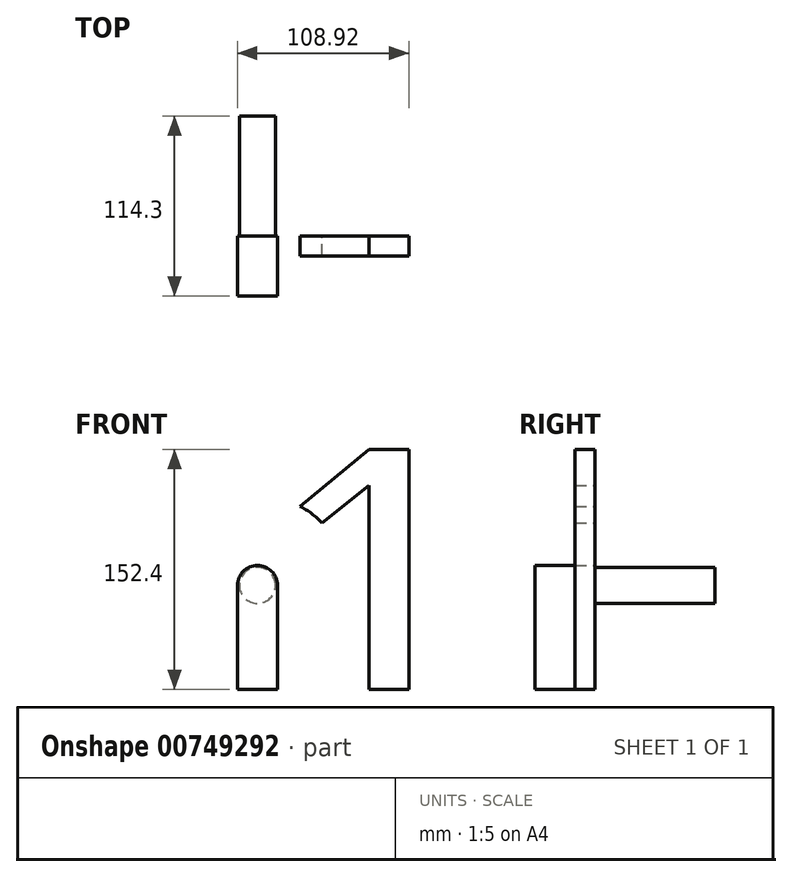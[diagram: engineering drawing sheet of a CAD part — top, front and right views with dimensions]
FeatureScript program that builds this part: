
annotation { "Feature Type Name" : "Feature", "Feature Type Description" : "" }
export const myFeature = defineFeature(function(context is Context, id is Id, definition is map)
    precondition{}
    {
        {
            var Q0;
            Q0=qCreatedBy(makeId("Front.planeOp"),FACE);
            var sketch = newSketch(context, id + "F0", { "sketchPlane" : qUnion([Q0])});
            skLineSegment(sketch, "E0", {"start": v(-9.03, 14.64) * mm, "end": v(34.6, 50.66) * mm});
            skLineSegment(sketch, "E1", {"start": v(4.97, 4) * mm, "end": v(49.46, 39.82) * mm});
            skLineSegment(sketch, "E2", {"start": v(34.6, 50.66) * mm, "end": v(34.6, -101.74) * mm});
            skLineSegment(sketch, "E3", {"start": v(34.6, -101.74) * mm, "end": v(60, -101.74) * mm});
            skLineSegment(sketch, "E4", {"start": v(60, -101.74) * mm, "end": v(60, 50.66) * mm});
            skLineSegment(sketch, "E5", {"start": v(60, 50.66) * mm, "end": v(34.6, 50.66) * mm});
            skArc(sketch, "E6", {"start": v(4.97, 4) * mm, "mid": v(-1.62, 9.86) * mm, "end": v(-9.03, 14.64) * mm});
            skPoint(sketch, "E7.orphan", {"position": v(-14.37, 10.24) * mm});
            skPoint(sketch, "E8.start.orphan", {"position": v(0, 0) * mm});
            skPoint(sketch, "E9.end.orphan", {"position": v(-72.43, -71.25) * mm});
            skArc(sketch, "E10", {"start": v(-72.43, -71.25) * mm, "mid": v(-0.59, -71.84) * mm, "end": v(0, 0) * mm});
            skCircle(sketch, "E11", {"center": v(-36.21, -35.63) * mm, "radius": 12.7 * mm});
            skLineSegment(sketch, "E12", {"start": v(34.6, -101.74) * mm, "end": v(-36.21, -101.74) * mm});
            skLineSegment(sketch, "E13", {"start": v(-36.21, -101.74) * mm, "end": v(-36.21, -47.06) * mm});
            skLineSegment(sketch, "E14", {"start": v(-48.91, -35.63) * mm, "end": v(-48.91, -101.74) * mm});
            skLineSegment(sketch, "E15", {"start": v(-48.91, -101.74) * mm, "end": v(-36.21, -101.74) * mm});
            skLineSegment(sketch, "E16", {"start": v(-23.51, -35.63) * mm, "end": v(-23.51, -101.74) * mm});
            skLineSegment(sketch, "E17", {"start": v(-48.91, -35.63) * mm, "end": v(-47.64, -35.63) * mm});
            skCircle(sketch, "E18", {"center": v(-36.21, -35.63) * mm, "radius": 11.43 * mm});
            skLineSegment(sketch, "E19.trimOffspring", {"start": v(-24.78, -35.63) * mm, "end": v(-23.51, -35.63) * mm});
            skSolve(sketch);
        }
        {
            var Q0;
            Q0 = qSketchRegion(id + "F0", true);
            extrude(context, id + "F1", {"entities" : qUnion([Q0]), "depth" : 12.7 * mm, "offsetDistance" : 25.4 * mm});
        }
        {
            var Q0;
            {var subQ5=sQuery(id+"F0.wireOp",EDGE,"E15");Q0=makeQuery(id+"F0.imprint","IMPRINT",FACE,{"disambiguationData":[TD([[makeQuery(id+"F0.imprint","IMPRINT",EDGE,{"derivedFrom":subQ5}),1.0]])]});}
            var Q1;
            {var subQ0=sQuery(id+"F0.wireOp",EDGE,"E16");var subQ1=sQuery(id+"F0.wireOp",EDGE,"E10");var subQ2=makeQuery(id+"F0.imprint","INTERSECT",VERTEX,{"derivedFrom":[subQ1,subQ0]});Q1=makeQuery(id+"F0.imprint","IMPRINT",FACE,{"disambiguationData":[TD([[makeQuery(id+"F0.imprint","IMPRINT",EDGE,{"disambiguationData":[TD([[subQ2,1.0]])],"derivedFrom":subQ1}),-1.0]])]});}
            var Q2;
            {var subQ0=sQuery(id+"F0.wireOp",EDGE,"E16");var subQ1=sQuery(id+"F0.wireOp",EDGE,"E10");var subQ2=makeQuery(id+"F0.imprint","INTERSECT",VERTEX,{"derivedFrom":[subQ1,subQ0]});Q2=makeQuery(id+"F0.imprint","IMPRINT",FACE,{"disambiguationData":[TD([[makeQuery(id+"F0.imprint","IMPRINT",EDGE,{"disambiguationData":[TD([[subQ2,1.0]])],"derivedFrom":subQ1}),1.0]])]});}
            var Q3;
            {var subQ0=sQuery(id+"F0.wireOp",EDGE,"E14");var subQ1=sQuery(id+"F0.wireOp",EDGE,"E10");var subQ2=makeQuery(id+"F0.imprint","INTERSECT",VERTEX,{"derivedFrom":[subQ1,subQ0]});Q3=makeQuery(id+"F0.imprint","IMPRINT",FACE,{"disambiguationData":[TD([[makeQuery(id+"F0.imprint","IMPRINT",EDGE,{"disambiguationData":[TD([[subQ2,-1.0]])],"derivedFrom":subQ1}),1.0]])]});}
            var Q4;
            {var subQ1=sQuery(id+"F0.wireOp",EDGE,"E11");var subQ3=sQuery(id+"F0.wireOp",EDGE,"E13");var subQ4=makeQuery(id+"F0.imprint","INTERSECT",VERTEX,{"derivedFrom":[subQ1,subQ3]});Q4=makeQuery(id+"F0.imprint","IMPRINT",FACE,{"disambiguationData":[TD([[makeQuery(id+"F0.imprint","IMPRINT",EDGE,{"disambiguationData":[TD([[subQ4,-1.0]])],"derivedFrom":subQ3}),1.0]])]});}
            var Q5;
            {var subQ1=sQuery(id+"F0.wireOp",EDGE,"E11");var subQ3=sQuery(id+"F0.wireOp",EDGE,"E13");var subQ4=makeQuery(id+"F0.imprint","INTERSECT",VERTEX,{"derivedFrom":[subQ1,subQ3]});Q5=makeQuery(id+"F0.imprint","IMPRINT",FACE,{"disambiguationData":[TD([[makeQuery(id+"F0.imprint","IMPRINT",EDGE,{"disambiguationData":[TD([[subQ4,-1.0]])],"derivedFrom":subQ3}),-1.0]])]});}
            var Q6;
            Q6=makeQuery(id+"F1.opExtrude","CAP_FACE",FACE,{"disambiguationData":[OSD([sQuery(id+"F0.wireOp",EDGE,"E11"),sQuery(id+"F0.wireOp",EDGE,"E12"),sQuery(id+"F0.wireOp",EDGE,"E14"),sQuery(id+"F0.wireOp",EDGE,"E15"),sQuery(id+"F0.wireOp",EDGE,"E16"),sQuery(id+"F0.wireOp",EDGE,"E18")])],"isStart":false});
            extrude(context, id + "F2", {"entities" : qUnion([Q0, Q1, Q2, Q3, Q4, Q5, Q6]), "operationType" : NewBodyOperationType.ADD, "depth" : 25.4 * mm, "offsetDistance" : 25.4 * mm});
        }
        {
            var Q0;
            {var subQ0=sQuery(id+"F0.wireOp",EDGE,"E18");var subQ1=makeQuery(id+"F0.imprint","INTERSECT",VERTEX,{"derivedFrom":[sQuery(id+"F0.wireOp",EDGE,"E17"),subQ0]});Q0=makeQuery(id+"F0.imprint","IMPRINT",FACE,{"disambiguationData":[TD([[makeQuery(id+"F0.imprint","IMPRINT",EDGE,{"disambiguationData":[TD([[subQ1,1.0]])],"derivedFrom":subQ0}),1.0]])]});}
            extrude(context, id + "F3", {"entities" : qUnion([Q0]), "operationType" : NewBodyOperationType.ADD, "depth" : 38.1 * mm, "offsetDistance" : 25.4 * mm, "hasSecondDirection" : true, "secondDirectionOppositeDirection" : true, "secondDirectionDepth" : 76.2 * mm});
        }
    });
